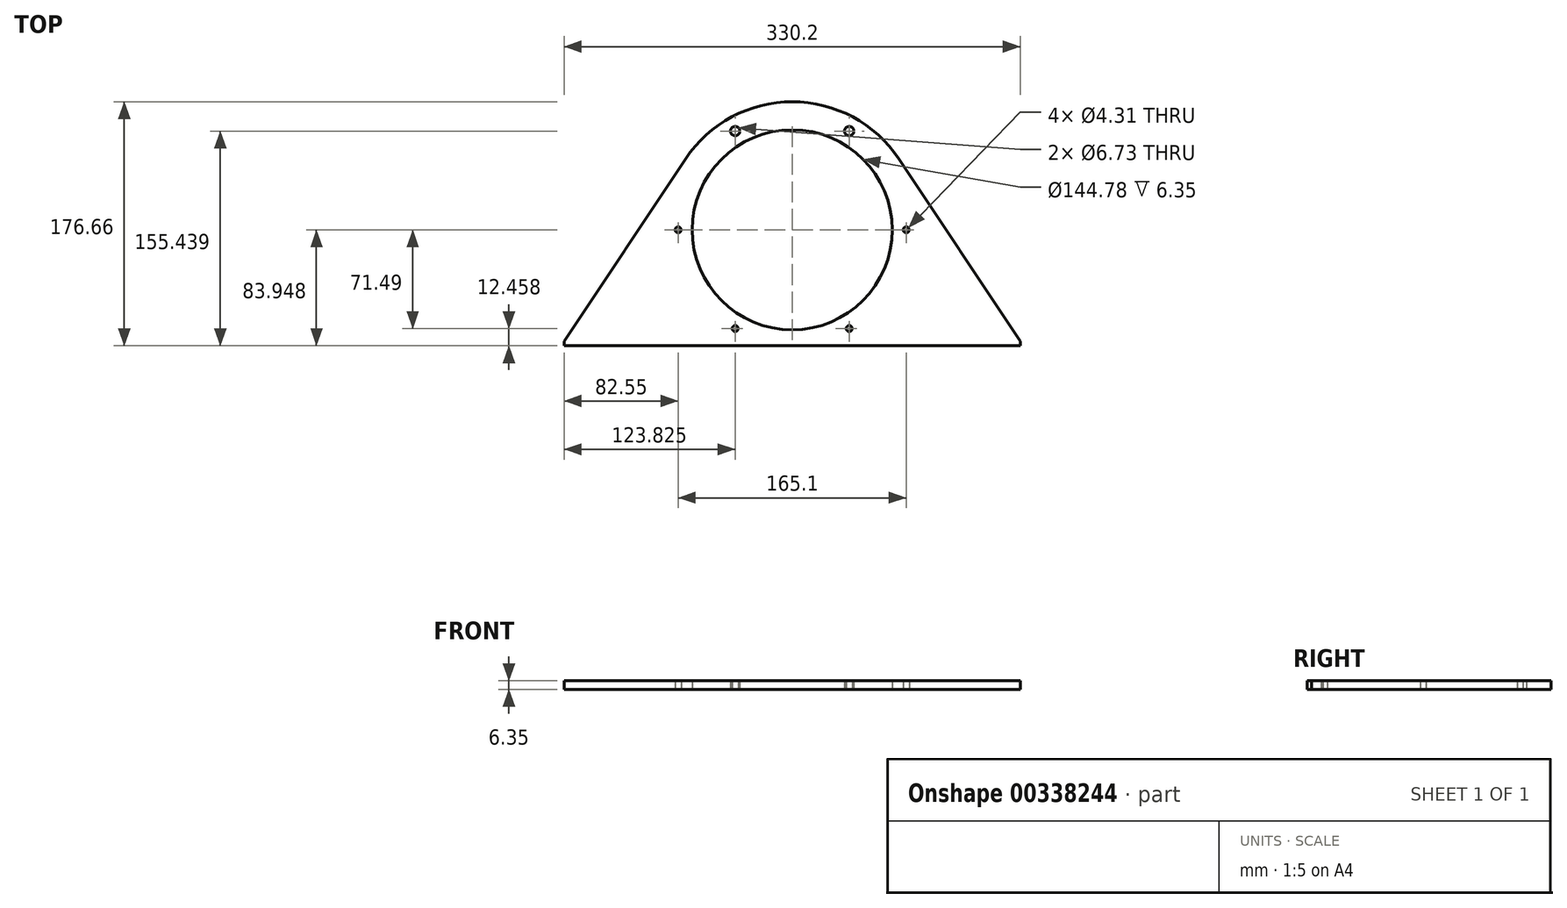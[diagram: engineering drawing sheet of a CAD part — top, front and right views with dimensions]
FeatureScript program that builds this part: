
annotation { "Feature Type Name" : "Feature", "Feature Type Description" : "" }
export const myFeature = defineFeature(function(context is Context, id is Id, definition is map)
    precondition{}
    {
        {
            var Q0;
            Q0=qCreatedBy(makeId("Top.planeOp"),FACE);
            var sketch = newSketch(context, id + "F0", { "sketchPlane" : qUnion([Q0])});
            skLineSegment(sketch, "E0", {"start": v(0, 0) * mm, "end": v(330.2, 0) * mm});
            skLineSegment(sketch, "E1", {"start": v(330.2, 0) * mm, "end": v(330.2, 3.17) * mm});
            skLineSegment(sketch, "E2", {"start": v(330.2, 3.17) * mm, "end": v(242.29, 135.3) * mm});
            skLineSegment(sketch, "E3", {"start": v(165.1, 0) * mm, "end": v(165.1, 83.95) * mm, "construction": true});
            skCircle(sketch, "E4", {"center": v(165.1, 83.95) * mm, "radius": 72.4 * mm});
            skArc(sketch, "E5", {"start": v(242.29, 135.3) * mm, "mid": v(165.1, 176.66) * mm, "end": v(87.91, 135.3) * mm});
            skLineSegment(sketch, "E6", {"start": v(165.1, 83.95) * mm, "end": v(247.65, 83.95) * mm, "construction": true});
            skLineSegment(sketch, "E7", {"start": v(165.1, 83.95) * mm, "end": v(123.82, 155.44) * mm, "construction": true});
            skLineSegment(sketch, "E8", {"start": v(165.1, 83.95) * mm, "end": v(206.38, 155.44) * mm, "construction": true});
            skLineSegment(sketch, "E9", {"start": v(165.1, 83.95) * mm, "end": v(165.1, 155.44) * mm, "construction": true});
            skLineSegment(sketch, "E10", {"start": v(123.83, 155.44) * mm, "end": v(206.37, 155.44) * mm, "construction": true});
            skCircle(sketch, "E11", {"center": v(123.83, 155.44) * mm, "radius": 10.16 * mm, "construction": true});
            skLineSegment(sketch, "E12", {"start": v(0, 0) * mm, "end": v(0, 3.17) * mm});
            skLineSegment(sketch, "E13", {"start": v(0, 3.17) * mm, "end": v(87.91, 135.3) * mm});
            skLineSegment(sketch, "E14", {"start": v(165.1, 83.95) * mm, "end": v(206.37, 12.46) * mm, "construction": true});
            skLineSegment(sketch, "E15", {"start": v(206.37, 12.46) * mm, "end": v(247.65, 83.95) * mm, "construction": true});
            skLineSegment(sketch, "E16", {"start": v(247.65, 83.95) * mm, "end": v(206.38, 155.44) * mm, "construction": true});
            skLineSegment(sketch, "E17", {"start": v(123.83, 155.44) * mm, "end": v(82.55, 83.95) * mm, "construction": true});
            skLineSegment(sketch, "E18", {"start": v(82.55, 83.95) * mm, "end": v(165.1, 83.95) * mm, "construction": true});
            skLineSegment(sketch, "E19", {"start": v(165.1, 83.95) * mm, "end": v(123.83, 12.46) * mm, "construction": true});
            skLineSegment(sketch, "E20", {"start": v(123.83, 12.46) * mm, "end": v(82.55, 83.95) * mm, "construction": true});
            skCircle(sketch, "E21", {"center": v(123.83, 155.44) * mm, "radius": 3.37 * mm});
            skCircle(sketch, "E22", {"center": v(206.37, 155.44) * mm, "radius": 3.37 * mm});
            skCircle(sketch, "E23", {"center": v(82.55, 83.95) * mm, "radius": 2.15 * mm});
            skCircle(sketch, "E24", {"center": v(123.83, 12.46) * mm, "radius": 2.15 * mm});
            skCircle(sketch, "E25", {"center": v(206.37, 12.46) * mm, "radius": 2.15 * mm});
            skCircle(sketch, "E26", {"center": v(247.65, 83.95) * mm, "radius": 2.15 * mm});
            skSolve(sketch);
        }
        {
            var Q0;
            Q0 = qSketchRegion(id + "F0", true);
            extrude(context, id + "F1", {"entities" : qUnion([Q0]), "depth" : 6.35 * mm});
        }
    });
